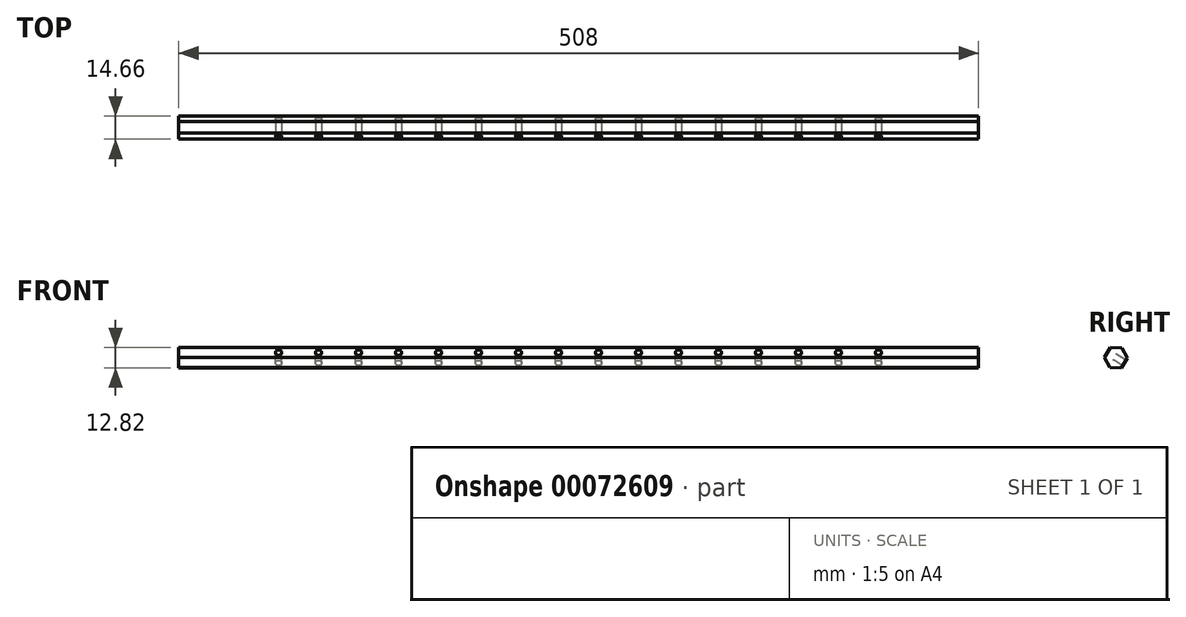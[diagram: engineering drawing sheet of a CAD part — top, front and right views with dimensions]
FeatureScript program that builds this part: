
annotation { "Feature Type Name" : "Feature", "Feature Type Description" : "" }
export const myFeature = defineFeature(function(context is Context, id is Id, definition is map)
    precondition{}
    {
        {
            var Q0;
            Q0=qCreatedBy(makeId("Right.planeOp"),FACE);
            var sketch = newSketch(context, id + "F0", { "sketchPlane" : qUnion([Q0])});
            skCircle(sketch, "E0.cCircle", {"center": v(0, 0) * mm, "radius": 6.35 * mm, "construction": true});
            skLineSegment(sketch, "E0.0", {"start": v(7.33, -0.12) * mm, "end": v(3.56, -6.4) * mm});
            skLineSegment(sketch, "E0.1", {"start": v(3.56, -6.4) * mm, "end": v(-3.77, -6.3) * mm});
            skLineSegment(sketch, "E0.2", {"start": v(-3.77, -6.3) * mm, "end": v(-7.33, 0.12) * mm});
            skLineSegment(sketch, "E0.3", {"start": v(-7.33, 0.12) * mm, "end": v(-3.56, 6.4) * mm});
            skLineSegment(sketch, "E0.4", {"start": v(-3.56, 6.4) * mm, "end": v(3.77, 6.3) * mm});
            skLineSegment(sketch, "E0.5", {"start": v(3.77, 6.3) * mm, "end": v(7.33, -0.12) * mm});
            skPoint(sketch, "E0.0.midPoint", {"position": v(5.45, -3.26) * mm});
            skSolve(sketch);
        }
        {
            var Q0;
            Q0=makeQuery(id+"F0.imprint","IMPRINT",FACE,{"disambiguationData":[TD([[makeQuery(id+"F0.imprint","IMPRINT",EDGE,{"derivedFrom":sQuery(id+"F0.wireOp",EDGE,"E0.0")}),-1.0]])]});
            extrude(context, id + "F1", {"entities" : qUnion([Q0]), "depth" : 508 * mm});
        }
        {
            var Q0;
            Q0=makeQuery(id+"F1.opExtrude","SWEPT_FACE",FACE,{"disambiguationData":[OSD([sQuery(id+"F0.wireOp",EDGE,"E0.3")])]});
            var sketch = newSketch(context, id + "F2", { "sketchPlane" : qUnion([Q0])});
            skPoint(sketch, "E1", {"position": v(241.3, 0) * mm});
            skPoint(sketch, "E2.1.0.0", {"position": v(266.7, 0) * mm});
            skPoint(sketch, "E2.2.0.0", {"position": v(292.1, 0) * mm});
            skPoint(sketch, "E2.3.0.0", {"position": v(317.5, 0) * mm});
            skPoint(sketch, "E2.4.0.0", {"position": v(342.9, 0) * mm});
            skPoint(sketch, "E2.5.0.0", {"position": v(368.3, 0) * mm});
            skPoint(sketch, "E2.6.0.0", {"position": v(393.7, 0) * mm});
            skPoint(sketch, "E2.7.0.0", {"position": v(419.1, 0) * mm});
            skLineSegment(sketch, "E2.direction1", {"start": v(241.3, 0) * mm, "end": v(266.7, 0) * mm, "construction": true});
            skPoint(sketch, "E3.1.0.0", {"position": v(215.9, 0) * mm});
            skPoint(sketch, "E3.2.0.0", {"position": v(190.5, 0) * mm});
            skPoint(sketch, "E3.3.0.0", {"position": v(165.1, 0) * mm});
            skPoint(sketch, "E3.4.0.0", {"position": v(139.7, 0) * mm});
            skPoint(sketch, "E3.5.0.0", {"position": v(114.3, 0) * mm});
            skPoint(sketch, "E3.6.0.0", {"position": v(88.9, 0) * mm});
            skPoint(sketch, "E3.7.0.0", {"position": v(63.5, 0) * mm});
            skLineSegment(sketch, "E3.direction1", {"start": v(241.3, 0) * mm, "end": v(215.9, 0) * mm, "construction": true});
            skPoint(sketch, "E4.0.8.0", {"position": v(444.5, 0) * mm});
            skSolve(sketch);
        }
        {
            var Q0;
            Q0=sQuery(id+"F2.wireOp",VERTEX,"E3.7.0.0");
            var Q1;
            Q1=sQuery(id+"F2.wireOp",VERTEX,"E3.6.0.0");
            var Q2;
            Q2=sQuery(id+"F2.wireOp",VERTEX,"E3.5.0.0");
            var Q3;
            Q3=sQuery(id+"F2.wireOp",VERTEX,"E3.4.0.0");
            var Q4;
            Q4=sQuery(id+"F2.wireOp",VERTEX,"E3.3.0.0");
            var Q5;
            Q5=sQuery(id+"F2.wireOp",VERTEX,"E3.2.0.0");
            var Q6;
            Q6=sQuery(id+"F2.wireOp",VERTEX,"E3.1.0.0");
            var Q7;
            Q7=sQuery(id+"F2.wireOp",VERTEX,"E1");
            var Q8;
            Q8=sQuery(id+"F2.wireOp",VERTEX,"E2.1.0.0");
            var Q9;
            Q9=sQuery(id+"F2.wireOp",VERTEX,"E2.2.0.0");
            var Q10;
            Q10=sQuery(id+"F2.wireOp",VERTEX,"E2.3.0.0");
            var Q11;
            Q11=sQuery(id+"F2.wireOp",VERTEX,"E2.4.0.0");
            var Q12;
            Q12=sQuery(id+"F2.wireOp",VERTEX,"E2.5.0.0");
            var Q13;
            Q13=sQuery(id+"F2.wireOp",VERTEX,"E2.6.0.0");
            var Q14;
            Q14=sQuery(id+"F2.wireOp",VERTEX,"E2.7.0.0");
            var Q15;
            Q15=sQuery(id+"F2.wireOp",VERTEX,"E4.0.8.0");
            var Q16;
            Q16=makeQuery(id+"F1.opExtrude","SWEPT_BODY",BODY,{"disambiguationData":[OSD([sQuery(id+"F0.wireOp",EDGE,"E0.0"),sQuery(id+"F0.wireOp",EDGE,"E0.1"),sQuery(id+"F0.wireOp",EDGE,"E0.2"),sQuery(id+"F0.wireOp",EDGE,"E0.3"),sQuery(id+"F0.wireOp",EDGE,"E0.4"),sQuery(id+"F0.wireOp",EDGE,"E0.5")])]});
            hole(context, id + "F3", {"style" : HoleStyle.SIMPLE, "holeDiameter" : 3.97 * mm, "endStyle" : HoleEndStyle.THROUGH, "locations" : qUnion([Q0, Q1, Q2, Q3, Q4, Q5, Q6, Q7, Q8, Q9, Q10, Q11, Q12, Q13, Q14, Q15]), "scope" : qUnion([Q16])});
        }
    });
